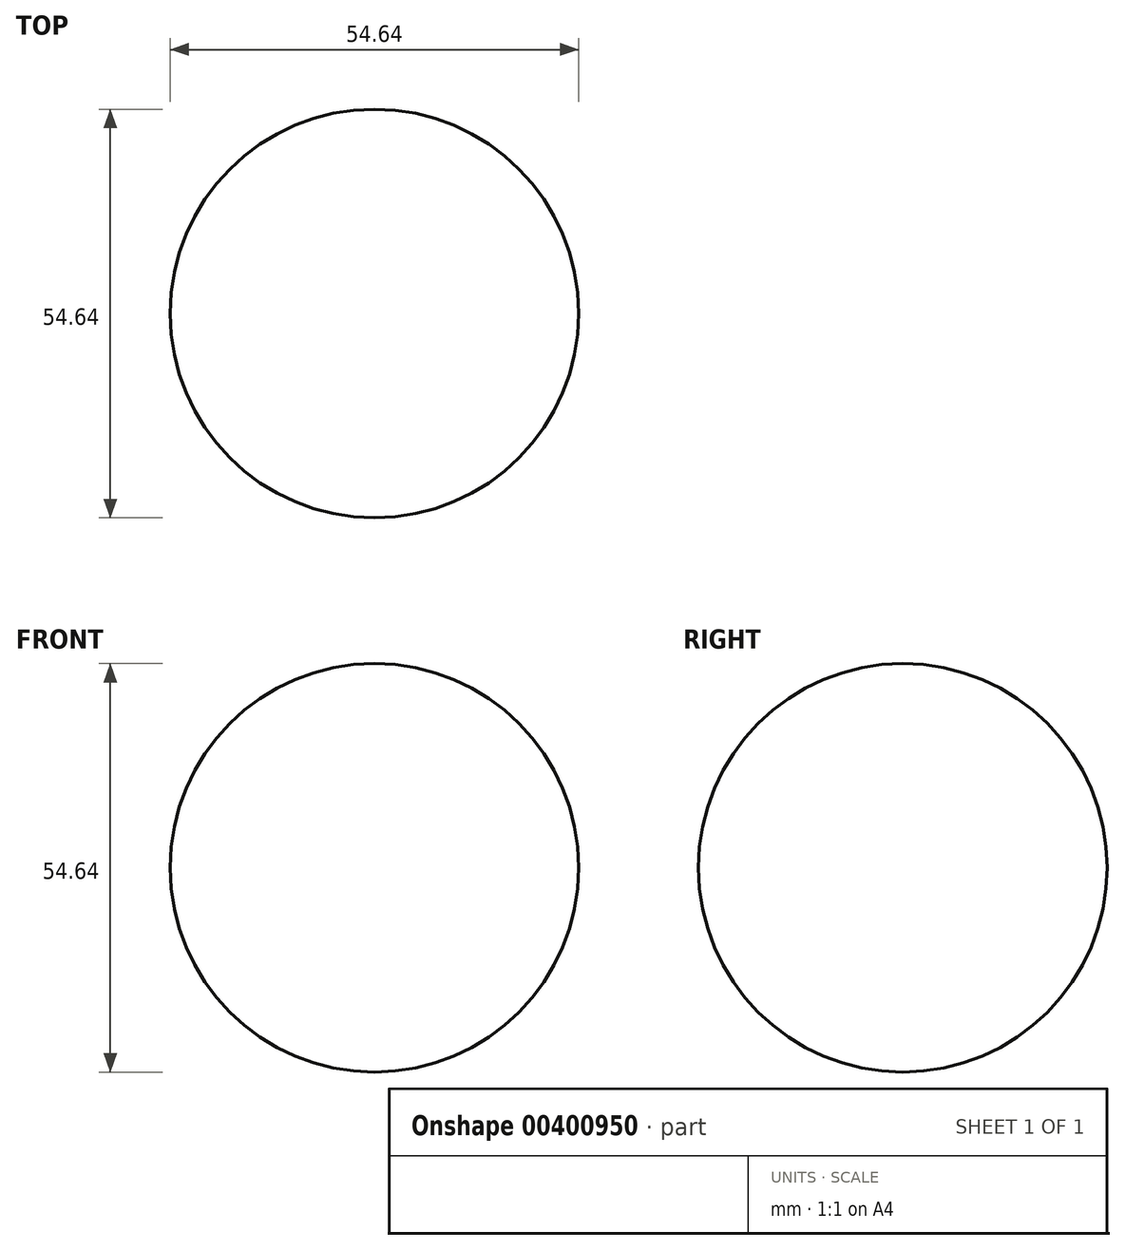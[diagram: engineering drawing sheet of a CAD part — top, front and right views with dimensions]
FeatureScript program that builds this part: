
annotation { "Feature Type Name" : "Feature", "Feature Type Description" : "" }
export const myFeature = defineFeature(function(context is Context, id is Id, definition is map)
    precondition{}
    {
        {
            var Q0;
            Q0=qCreatedBy(makeId("Front.planeOp"),FACE);
            var sketch = newSketch(context, id + "F0", { "sketchPlane" : qUnion([Q0])});
            skLineSegment(sketch, "E0", {"start": v(-112.85, 0) * mm, "end": v(121.24, 0) * mm, "construction": true});
            skLineSegment(sketch, "E1", {"start": v(-61.55, 0) * mm, "end": v(61.55, 0) * mm});
            skCircle(sketch, "E2", {"center": v(0, 0) * mm, "radius": 27.32 * mm});
            skSolve(sketch);
        }
        {
            var Q0;
            {var subQ0=sQuery(id+"F0.wireOp",EDGE,"E2");var subQ1=sQuery(id+"F0.wireOp",EDGE,"E1");var subQ2=makeQuery(id+"F0.imprint","INTERSECT",VERTEX,{"disambiguationData":[OD(0.0)],"derivedFrom":[subQ1,subQ0]});Q0=makeQuery(id+"F0.imprint","IMPRINT",FACE,{"disambiguationData":[TD([[makeQuery(id+"F0.imprint","IMPRINT",EDGE,{"disambiguationData":[TD([[subQ2,-1.0]])],"derivedFrom":subQ1}),1.0]])]});}
            var Q1;
            Q1=sQuery(id+"F0.wireOp",EDGE,"E0");
            revolve(context, id + "F1", {"entities" : qUnion([Q0]), "axis" : qUnion([Q1]), "revolveType" : RevolveType.FULL});
        }
    });
